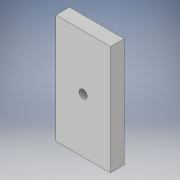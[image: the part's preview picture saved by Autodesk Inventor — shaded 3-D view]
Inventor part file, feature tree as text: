
AUTODESK INVENTOR PART (.ipt)
format: ipt  version: 2019 (Build 230136000, 136)  size: 106,496 bytes
history: native  units: mm
features: sketch x2, other x1, extrude x1, hole x1
ambient origin geometry x8: Origin, YZ Plane, XZ Plane, XY Plane, X Axis, Y Axis, Z Axis, Center Point
bodies: Body1 (feature_tree)
feature tree (5):
  other  "ソリッド1"
  extrude  "押し出し1"  Depth=40.0mm
  hole  "穴1"  [1 undecoded]
  sketch  "スケッチ1"
  sketch  "スケッチ2"
note: 1 required parameter value undecoded (feature->parameter linkage not recoverable at this tier; creation-order binding heuristic only, values carry confidence <= 0.55)
